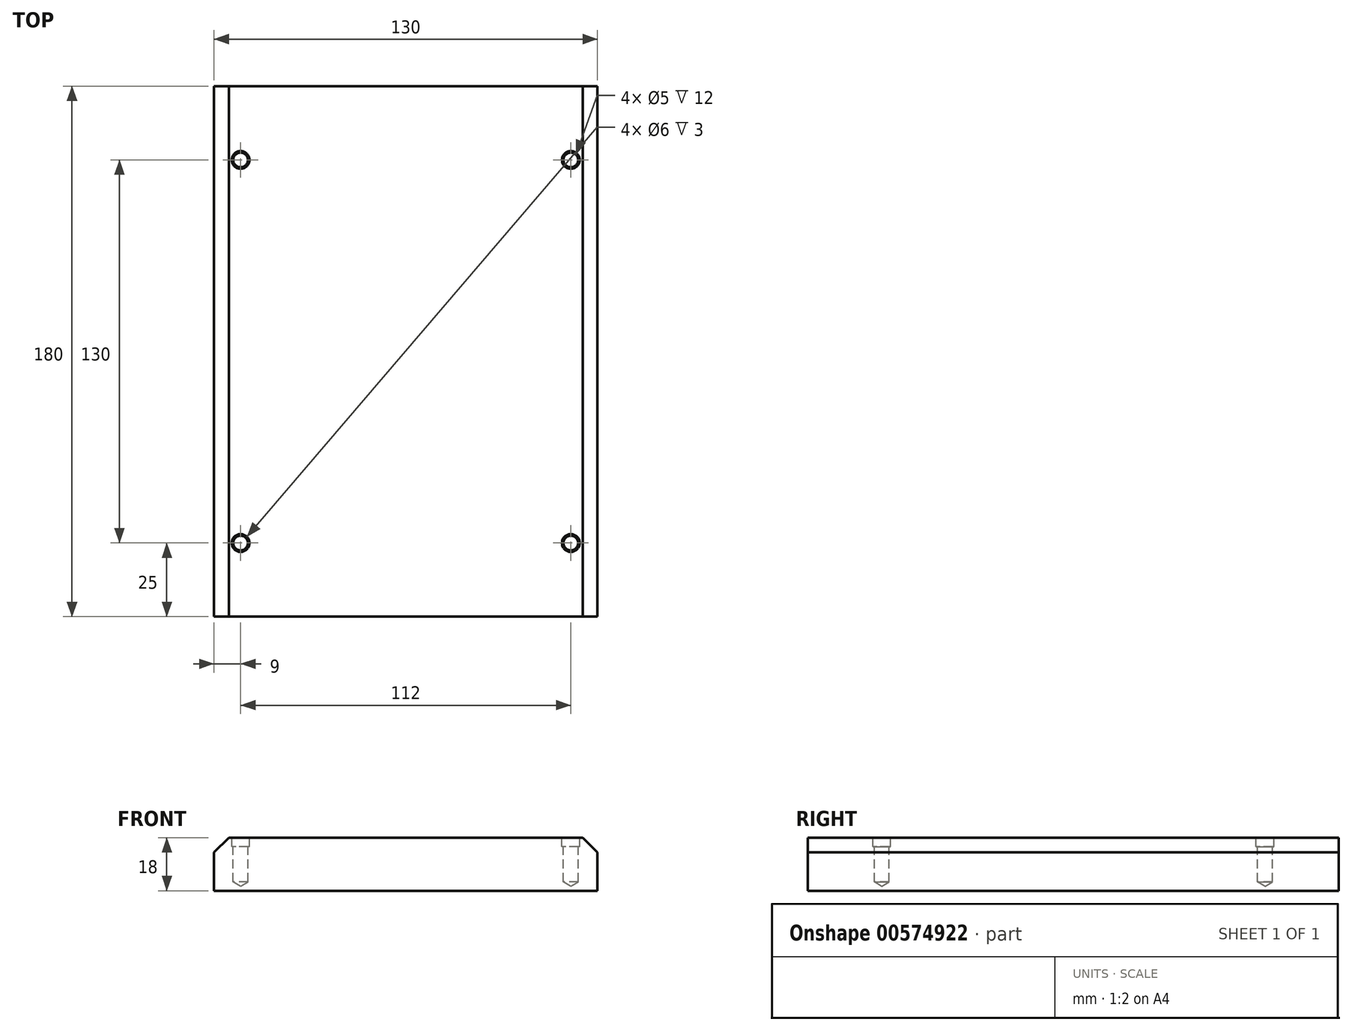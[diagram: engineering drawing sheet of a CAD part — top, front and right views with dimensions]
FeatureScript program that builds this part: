
annotation { "Feature Type Name" : "Feature", "Feature Type Description" : "" }
export const myFeature = defineFeature(function(context is Context, id is Id, definition is map)
    precondition{}
    {
        {
            var Q0;
            Q0=qCreatedBy(makeId("Top.planeOp"),FACE);
            var sketch = newSketch(context, id + "F0", { "sketchPlane" : qUnion([Q0])});
            skLineSegment(sketch, "E0.bottom", {"start": v(65, 90) * mm, "end": v(-65, 90) * mm});
            skLineSegment(sketch, "E0.top", {"start": v(65, -90) * mm, "end": v(-65, -90) * mm});
            skLineSegment(sketch, "E0.left", {"start": v(65, 90) * mm, "end": v(65, -90) * mm});
            skLineSegment(sketch, "E0.right", {"start": v(-65, 90) * mm, "end": v(-65, -90) * mm});
            skPoint(sketch, "E0.middle", {"position": v(0, 0) * mm});
            skSolve(sketch);
        }
        {
            var Q0;
            Q0=makeQuery(id+"F0.imprint","IMPRINT",FACE,{"disambiguationData":[TD([[makeQuery(id+"F0.imprint","IMPRINT",EDGE,{"derivedFrom":sQuery(id+"F0.wireOp",EDGE,"E0.bottom")}),1.0]])]});
            extrude(context, id + "F1", {"entities" : qUnion([Q0]), "depth" : 18 * mm, "offsetDistance" : 25 * mm, "symmetric" : true});
        }
        {
            var Q0;
            Q0=makeQuery(id+"F1.opExtrude","CAP_FACE",FACE,{"disambiguationData":[OSD([sQuery(id+"F0.wireOp",EDGE,"E0.bottom"),sQuery(id+"F0.wireOp",EDGE,"E0.top"),sQuery(id+"F0.wireOp",EDGE,"E0.left"),sQuery(id+"F0.wireOp",EDGE,"E0.right")])],"isStart":false});
            var sketch = newSketch(context, id + "F2", { "sketchPlane" : qUnion([Q0])});
            skPoint(sketch, "E1", {"position": v(-56, 65) * mm});
            skPoint(sketch, "E2", {"position": v(56, 65) * mm});
            skPoint(sketch, "E3", {"position": v(56, -65) * mm});
            skPoint(sketch, "E4", {"position": v(-56, -65) * mm});
            skSolve(sketch);
        }
        {
            var Q0;
            Q0=sQuery(id+"F2.wireOp",VERTEX,"E1");
            var Q1;
            Q1=sQuery(id+"F2.wireOp",VERTEX,"E2");
            var Q2;
            Q2=sQuery(id+"F2.wireOp",VERTEX,"E3");
            var Q3;
            Q3=sQuery(id+"F2.wireOp",VERTEX,"E4");
            var Q4;
            Q4=makeQuery(id+"F1.opExtrude","SWEPT_BODY",BODY,{"disambiguationData":[OSD([sQuery(id+"F0.wireOp",EDGE,"E0.bottom"),sQuery(id+"F0.wireOp",EDGE,"E0.top"),sQuery(id+"F0.wireOp",EDGE,"E0.left"),sQuery(id+"F0.wireOp",EDGE,"E0.right")])]});
            hole(context, id + "F3", {"style" : HoleStyle.C_BORE, "endStyle" : HoleEndStyle.BLIND, "holeDiameter" : 5 * mm, "cBoreDiameter" : 6 * mm, "cBoreDepth" : 3 * mm, "holeDepth" : 15 * mm, "isTappedThrough" : true, "tappedDepth" : 12 * mm, "tapClearance" : 3, "locations" : qUnion([Q0, Q1, Q2, Q3]), "scope" : qUnion([Q4]), "majorDiameter" : 5 * mm});
        }
        {
            var Q0;
            Q0=makeQuery(id+"F1.opExtrude","CAP_EDGE",EDGE,{"disambiguationData":[OSD([sQuery(id+"F0.wireOp",EDGE,"E0.right")])],"isStart":false});
            var Q1;
            Q1=makeQuery(id+"F1.opExtrude","CAP_EDGE",EDGE,{"disambiguationData":[OSD([sQuery(id+"F0.wireOp",EDGE,"E0.left")])],"isStart":false});
            chamfer(context, id + "F4", {"entities" : qUnion([Q0, Q1]), "width" : 5 * mm, "tangentPropagation" : true});
        }
    });
